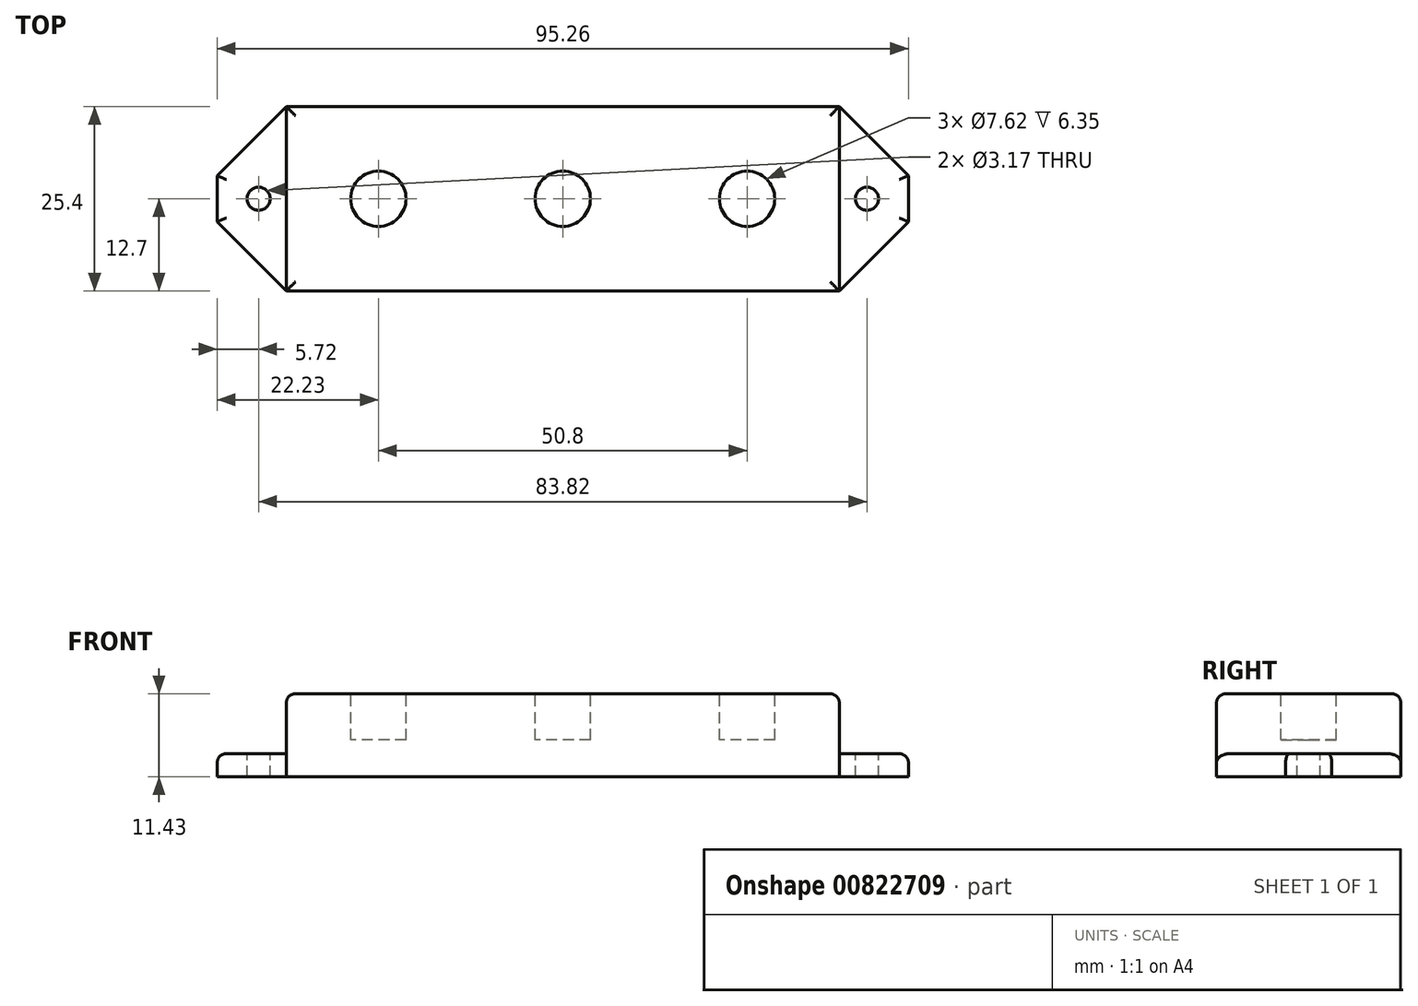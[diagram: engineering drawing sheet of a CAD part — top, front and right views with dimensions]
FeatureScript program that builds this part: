
annotation { "Feature Type Name" : "Feature", "Feature Type Description" : "" }
export const myFeature = defineFeature(function(context is Context, id is Id, definition is map)
    precondition{}
    {
        {
            var Q0;
            Q0=qCreatedBy(makeId("Top.planeOp"),FACE);
            var sketch = newSketch(context, id + "F0", { "sketchPlane" : qUnion([Q0])});
            skLineSegment(sketch, "E0", {"start": v(0, 0) * mm, "end": v(0, 25.4) * mm});
            skLineSegment(sketch, "E1", {"start": v(0, 25.4) * mm, "end": v(76.2, 25.4) * mm});
            skLineSegment(sketch, "E2", {"start": v(76.2, 25.4) * mm, "end": v(76.2, 0) * mm});
            skLineSegment(sketch, "E3", {"start": v(76.2, 0) * mm, "end": v(0, 0) * mm});
            skSolve(sketch);
        }
        {
            var Q0;
            Q0 = qSketchRegion(id + "F0", true);
            extrude(context, id + "F1", {"entities" : qUnion([Q0]), "depth" : 11.43 * mm, "offsetDistance" : 25.4 * mm});
        }
        {
            var Q0;
            Q0=makeQuery(id+"F1.opExtrude","CAP_FACE",FACE,{"disambiguationData":[OSD([sQuery(id+"F0.wireOp",EDGE,"E0"),sQuery(id+"F0.wireOp",EDGE,"E1"),sQuery(id+"F0.wireOp",EDGE,"E2"),sQuery(id+"F0.wireOp",EDGE,"E3")])],"isStart":false});
            var sketch = newSketch(context, id + "F2", { "sketchPlane" : qUnion([Q0])});
            skCircle(sketch, "E4", {"center": v(12.7, 12.7) * mm, "radius": 3.81 * mm});
            skCircle(sketch, "E5", {"center": v(38.1, 12.7) * mm, "radius": 3.81 * mm});
            skCircle(sketch, "E6", {"center": v(63.5, 12.7) * mm, "radius": 3.81 * mm});
            skSolve(sketch);
        }
        {
            var Q0;
            Q0 = qSketchRegion(id + "F2", true);
            extrude(context, id + "F3", {"entities" : qUnion([Q0]), "operationType" : NewBodyOperationType.REMOVE, "oppositeDirection" : true, "depth" : 6.35 * mm, "offsetDistance" : 25.4 * mm});
        }
        {
            var Q0;
            Q0=makeQuery(id+"F1.opExtrude","CAP_EDGE",EDGE,{"disambiguationData":[OSD([sQuery(id+"F0.wireOp",EDGE,"E3")])],"isStart":false});
            var Q1;
            Q1=makeQuery(id+"F1.opExtrude","CAP_EDGE",EDGE,{"disambiguationData":[OSD([sQuery(id+"F0.wireOp",EDGE,"E2")])],"isStart":false});
            var Q2;
            Q2=makeQuery(id+"F1.opExtrude","CAP_EDGE",EDGE,{"disambiguationData":[OSD([sQuery(id+"F0.wireOp",EDGE,"E1")])],"isStart":false});
            var Q3;
            Q3=makeQuery(id+"F1.opExtrude","CAP_EDGE",EDGE,{"disambiguationData":[OSD([sQuery(id+"F0.wireOp",EDGE,"E0")])],"isStart":false});
            fillet(context, id + "F4", {"entities" : qUnion([Q0, Q1, Q2, Q3]), "radius" : 1.27 * mm, "tangentPropagation" : true, "allowEdgeOverflow" : false});
        }
        {
            var Q0;
            Q0=makeQuery(id+"F1.opExtrude","SWEPT_FACE",FACE,{"disambiguationData":[OSD([sQuery(id+"F0.wireOp",EDGE,"E2")])]});
            var sketch = newSketch(context, id + "F5", { "sketchPlane" : qUnion([Q0])});
            skLineSegment(sketch, "E7", {"start": v(25.4, 3.18) * mm, "end": v(0, 3.17) * mm});
            skSolve(sketch);
        }
        {
            var Q0;
            Q0 = qSketchRegion(id + "F5", true);
            var Q1;
            {var subQ0=sQuery(id+"F5.wireOp",EDGE,"E7");Q1=makeQuery(id+"F5.imprint","IMPRINT",FACE,{"disambiguationData":[TD([[makeQuery(id+"F5.imprint","IMPRINT",EDGE,{"derivedFrom":subQ0}),1.0]])]});}
            extrude(context, id + "F6", {"entities" : qUnion([Q0, Q1]), "operationType" : NewBodyOperationType.ADD, "depth" : 9.52 * mm, "offsetDistance" : 25.4 * mm});
        }
        {
            var Q0;
            Q0=makeQuery(id+"F1.opExtrude","SWEPT_FACE",FACE,{"disambiguationData":[OSD([sQuery(id+"F0.wireOp",EDGE,"E0")])]});
            var sketch = newSketch(context, id + "F7", { "sketchPlane" : qUnion([Q0])});
            skLineSegment(sketch, "E8", {"start": v(-25.4, 3.18) * mm, "end": v(0, 3.18) * mm});
            skSolve(sketch);
        }
        {
            var Q0;
            Q0 = qSketchRegion(id + "F7", true);
            var Q1;
            {var subQ0=sQuery(id+"F7.wireOp",EDGE,"E8");Q1=makeQuery(id+"F7.imprint","IMPRINT",FACE,{"disambiguationData":[TD([[makeQuery(id+"F7.imprint","IMPRINT",EDGE,{"derivedFrom":subQ0}),-1.0]])]});}
            extrude(context, id + "F8", {"entities" : qUnion([Q0, Q1]), "operationType" : NewBodyOperationType.ADD, "depth" : 9.52 * mm, "offsetDistance" : 25.4 * mm});
        }
        {
            var Q0;
            Q0=makeQuery(id+"F8.opExtrude","CAP_EDGE",EDGE,{"disambiguationData":[OSD([sQuery(id+"F0.wireOp",EDGE,"E0"),sQuery(id+"F0.wireOp",EDGE,"E3")])],"isStart":false});
            var Q1;
            Q1=makeQuery(id+"F8.opExtrude","CAP_EDGE",EDGE,{"disambiguationData":[OSD([sQuery(id+"F0.wireOp",EDGE,"E0"),sQuery(id+"F0.wireOp",EDGE,"E1")])],"isStart":false});
            var Q2;
            Q2=makeQuery(id+"F6.opExtrude","CAP_EDGE",EDGE,{"disambiguationData":[OSD([sQuery(id+"F0.wireOp",EDGE,"E2"),sQuery(id+"F0.wireOp",EDGE,"E3")])],"isStart":false});
            var Q3;
            Q3=makeQuery(id+"F6.opExtrude","CAP_EDGE",EDGE,{"disambiguationData":[OSD([sQuery(id+"F0.wireOp",EDGE,"E1"),sQuery(id+"F0.wireOp",EDGE,"E2")])],"isStart":false});
            chamfer(context, id + "F9", {"entities" : qUnion([Q0, Q1, Q2, Q3]), "width" : 9.52 * mm, "tangentPropagation" : true});
        }
        {
            var Q0;
            Q0=makeQuery(id+"F9.opChamfer","BLEND_EDGE",EDGE,{"blendedFrom":[makeQuery(id+"F8.opExtrude","CAP_EDGE",EDGE,{"disambiguationData":[OSD([sQuery(id+"F0.wireOp",EDGE,"E0"),sQuery(id+"F0.wireOp",EDGE,"E3")])],"isStart":false}),makeQuery(id+"F8.opExtrude","SWEPT_FACE",FACE,{"disambiguationData":[OSD([sQuery(id+"F7.wireOp",EDGE,"E8")])]})],"blendedInto":[makeQuery(id+"F8.opExtrude","SWEPT_FACE",FACE,{"disambiguationData":[OSD([sQuery(id+"F7.wireOp",EDGE,"E8")])]})]});
            var Q1;
            Q1=makeQuery(id+"F8.opExtrude","CAP_EDGE",EDGE,{"disambiguationData":[OSD([sQuery(id+"F7.wireOp",EDGE,"E8")])],"isStart":false});
            var Q2;
            Q2=makeQuery(id+"F9.opChamfer","BLEND_EDGE",EDGE,{"blendedFrom":[makeQuery(id+"F8.opExtrude","CAP_EDGE",EDGE,{"disambiguationData":[OSD([sQuery(id+"F0.wireOp",EDGE,"E0"),sQuery(id+"F0.wireOp",EDGE,"E1")])],"isStart":false}),makeQuery(id+"F8.opExtrude","SWEPT_FACE",FACE,{"disambiguationData":[OSD([sQuery(id+"F7.wireOp",EDGE,"E8")])]})],"blendedInto":[makeQuery(id+"F8.opExtrude","SWEPT_FACE",FACE,{"disambiguationData":[OSD([sQuery(id+"F7.wireOp",EDGE,"E8")])]})]});
            var Q3;
            Q3=makeQuery(id+"F9.opChamfer","BLEND_EDGE",EDGE,{"blendedFrom":[makeQuery(id+"F6.opExtrude","CAP_EDGE",EDGE,{"disambiguationData":[OSD([sQuery(id+"F0.wireOp",EDGE,"E2"),sQuery(id+"F0.wireOp",EDGE,"E3")])],"isStart":false}),makeQuery(id+"F6.opExtrude","SWEPT_FACE",FACE,{"disambiguationData":[OSD([sQuery(id+"F5.wireOp",EDGE,"E7")])]})],"blendedInto":[makeQuery(id+"F6.opExtrude","SWEPT_FACE",FACE,{"disambiguationData":[OSD([sQuery(id+"F5.wireOp",EDGE,"E7")])]})]});
            var Q4;
            Q4=makeQuery(id+"F6.opExtrude","CAP_EDGE",EDGE,{"disambiguationData":[OSD([sQuery(id+"F5.wireOp",EDGE,"E7")])],"isStart":false});
            var Q5;
            Q5=makeQuery(id+"F9.opChamfer","BLEND_EDGE",EDGE,{"blendedFrom":[makeQuery(id+"F6.opExtrude","CAP_EDGE",EDGE,{"disambiguationData":[OSD([sQuery(id+"F0.wireOp",EDGE,"E1"),sQuery(id+"F0.wireOp",EDGE,"E2")])],"isStart":false}),makeQuery(id+"F6.opExtrude","SWEPT_FACE",FACE,{"disambiguationData":[OSD([sQuery(id+"F5.wireOp",EDGE,"E7")])]})],"blendedInto":[makeQuery(id+"F6.opExtrude","SWEPT_FACE",FACE,{"disambiguationData":[OSD([sQuery(id+"F5.wireOp",EDGE,"E7")])]})]});
            fillet(context, id + "F10", {"entities" : qUnion([Q0, Q1, Q2, Q3, Q4, Q5]), "radius" : 1.27 * mm, "tangentPropagation" : true, "allowEdgeOverflow" : false});
        }
        {
            var Q0;
            Q0=makeQuery(id+"F8.opExtrude","SWEPT_FACE",FACE,{"disambiguationData":[OSD([sQuery(id+"F7.wireOp",EDGE,"E8")])]});
            var sketch = newSketch(context, id + "F11", { "sketchPlane" : qUnion([Q0])});
            skCircle(sketch, "E9", {"center": v(-3.81, 12.7) * mm, "radius": 1.59 * mm});
            skPoint(sketch, "E9.centerSnap0", {"position": v(-8.26, 12.7) * mm});
            skSolve(sketch);
        }
        {
            var Q0;
            Q0 = qSketchRegion(id + "F11", true);
            extrude(context, id + "F12", {"entities" : qUnion([Q0]), "operationType" : NewBodyOperationType.REMOVE, "oppositeDirection" : true, "depth" : 25.4 * mm, "offsetDistance" : 25.4 * mm});
        }
        {
            var Q0;
            Q0=makeQuery(id+"F6.opExtrude","SWEPT_FACE",FACE,{"disambiguationData":[OSD([sQuery(id+"F5.wireOp",EDGE,"E7")])]});
            var sketch = newSketch(context, id + "F13", { "sketchPlane" : qUnion([Q0])});
            skCircle(sketch, "E10", {"center": v(80, 12.7) * mm, "radius": 1.59 * mm});
            skPoint(sketch, "E10.centerSnap0", {"position": v(84.45, 12.7) * mm});
            skSolve(sketch);
        }
        {
            var Q0;
            Q0 = qSketchRegion(id + "F13", true);
            extrude(context, id + "F14", {"entities" : qUnion([Q0]), "operationType" : NewBodyOperationType.REMOVE, "oppositeDirection" : true, "depth" : 25.4 * mm, "offsetDistance" : 25.4 * mm});
        }
    });
